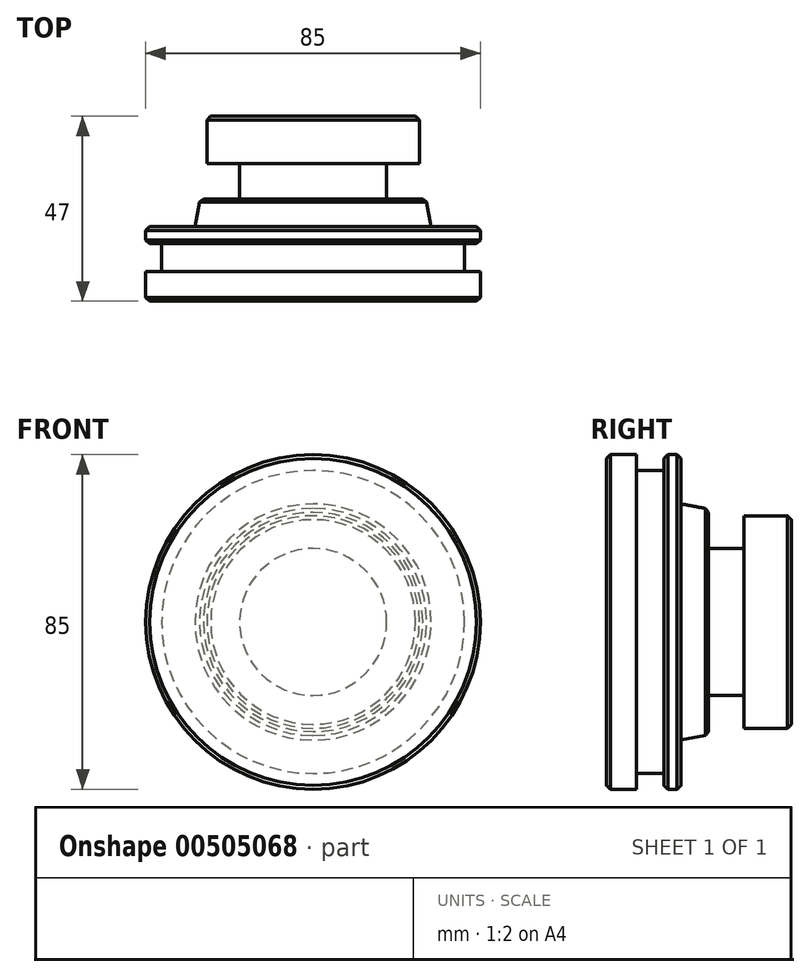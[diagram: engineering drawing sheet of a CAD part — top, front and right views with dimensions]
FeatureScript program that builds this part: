
annotation { "Feature Type Name" : "Feature", "Feature Type Description" : "" }
export const myFeature = defineFeature(function(context is Context, id is Id, definition is map)
    precondition{}
    {
        {
            var Q0;
            Q0=qCreatedBy(makeId("Front.planeOp"),FACE);
            var sketch = newSketch(context, id + "F0", { "sketchPlane" : qUnion([Q0])});
            skCircle(sketch, "E0", {"center": v(0, 0) * mm, "radius": 42.5 * mm});
            skSolve(sketch);
        }
        {
            var Q0;
            Q0 = qSketchRegion(id + "F0", true);
            extrude(context, id + "F1", {"entities" : qUnion([Q0]), "depth" : 19 * mm});
        }
        {
            var Q0;
            Q0=qCreatedBy(makeId("Right.planeOp"),FACE);
            var sketch = newSketch(context, id + "F2", { "sketchPlane" : qUnion([Q0])});
            skLineSegment(sketch, "E1", {"start": v(0, 0) * mm, "end": v(0, 42.5) * mm, "construction": true});
            skLineSegment(sketch, "E2", {"start": v(0, 42.5) * mm, "end": v(-4.4, 42.5) * mm, "construction": true});
            skLineSegment(sketch, "E3", {"start": v(-4.4, 42.5) * mm, "end": v(-4.4, 38.5) * mm});
            skLineSegment(sketch, "E4", {"start": v(-4.4, 38.5) * mm, "end": v(-11.4, 38.5) * mm});
            skLineSegment(sketch, "E5", {"start": v(-11.4, 38.5) * mm, "end": v(-11.4, 42.5) * mm});
            skLineSegment(sketch, "E6", {"start": v(0, 0) * mm, "end": v(-24.13, 0) * mm, "construction": true});
            skLineSegment(sketch, "E7", {"start": v(-11.4, 42.5) * mm, "end": v(-4.4, 42.5) * mm});
            skSolve(sketch);
        }
        {
            var Q0;
            Q0 = qSketchRegion(id + "F2", true);
            var Q1;
            Q1=makeQuery(id+"F1.opExtrude","SWEPT_FACE",FACE,{"disambiguationData":[OSD([sQuery(id+"F0.wireOp",EDGE,"E0")])]});
            revolve(context, id + "F3", {"operationType" : NewBodyOperationType.REMOVE, "entities" : qUnion([Q0]), "axis" : qUnion([Q1]), "revolveType" : RevolveType.FULL, "oppositeDirection" : true});
        }
        {
            var Q0;
            Q0=makeQuery(id+"F1.opExtrude","CAP_FACE",FACE,{"disambiguationData":[OSD([sQuery(id+"F0.wireOp",EDGE,"E0")])],"isStart":true});
            var sketch = newSketch(context, id + "F4", { "sketchPlane" : qUnion([Q0])});
            skCircle(sketch, "E8", {"center": v(0, 0) * mm, "radius": 30 * mm});
            skSolve(sketch);
        }
        {
            var Q0;
            Q0 = qSketchRegion(id + "F4", true);
            extrude(context, id + "F5", {"entities" : qUnion([Q0]), "operationType" : NewBodyOperationType.ADD, "depth" : 16 * mm});
        }
        {
            var Q0;
            Q0=makeQuery(id+"F5.opExtrude","CAP_FACE",FACE,{"disambiguationData":[OSD([sQuery(id+"F4.wireOp",EDGE,"E8")])],"isStart":false});
            var sketch = newSketch(context, id + "F6", { "sketchPlane" : qUnion([Q0])});
            skCircle(sketch, "E9", {"center": v(0, 0) * mm, "radius": 27 * mm});
            skSolve(sketch);
        }
        {
            var Q0;
            Q0 = qSketchRegion(id + "F6", true);
            extrude(context, id + "F7", {"entities" : qUnion([Q0]), "operationType" : NewBodyOperationType.ADD, "depth" : 12 * mm});
        }
        {
            var Q0;
            Q0=qCreatedBy(makeId("Top.planeOp"),FACE);
            var sketch = newSketch(context, id + "F8", { "sketchPlane" : qUnion([Q0])});
            skLineSegment(sketch, "E10", {"start": v(0, 0) * mm, "end": v(-30, 0) * mm, "construction": true});
            skLineSegment(sketch, "E11", {"start": v(0, 0) * mm, "end": v(0, 16) * mm, "construction": true});
            skLineSegment(sketch, "E12", {"start": v(0, 16) * mm, "end": v(-27, 16) * mm, "construction": true});
            skLineSegment(sketch, "E13", {"start": v(-30, 0) * mm, "end": v(-28.69, 7) * mm});
            skLineSegment(sketch, "E14", {"start": v(-30, 16) * mm, "end": v(-30, 0) * mm});
            skLineSegment(sketch, "E15", {"start": v(0, 0) * mm, "end": v(0, 46.41) * mm, "construction": true});
            skLineSegment(sketch, "E16", {"start": v(-27, 16) * mm, "end": v(-27, 7) * mm, "construction": true});
            skLineSegment(sketch, "E17", {"start": v(-28.69, 7) * mm, "end": v(-18.69, 7) * mm});
            skLineSegment(sketch, "E18", {"start": v(-18.69, 7) * mm, "end": v(-18.69, 16) * mm});
            skLineSegment(sketch, "E19", {"start": v(-18.69, 16) * mm, "end": v(-30, 16) * mm});
            skSolve(sketch);
        }
        {
            var Q0;
            Q0 = qSketchRegion(id + "F8", true);
            var Q1;
            Q1=sQuery(id+"F8.wireOp",EDGE,"E13");
            var Q2;
            Q2=sQuery(id+"F8.wireOp",EDGE,"E14");
            var Q3;
            Q3=sQuery(id+"F8.wireOp",EDGE,"Bem9fb8M-xfDn-7svO-rLqh-bTkrtEkM8QLy");
            var Q4;
            Q4=sQuery(id+"F8.wireOp",EDGE,"E15");
            revolve(context, id + "F9", {"operationType" : NewBodyOperationType.REMOVE, "entities" : qUnion([Q0]), "surfaceEntities" : qUnion([Q1, Q2, Q3]), "axis" : qUnion([Q4]), "revolveType" : RevolveType.FULL, "oppositeDirection" : true});
        }
        {
            var Q0;
            Q0=makeQuery(id+"F3.boolean.opBoolean","COPY",EDGE,{"derivedFrom":makeQuery(id+"F3.opRevolve","SWEPT_EDGE",EDGE,{"disambiguationData":[OSD([sQuery(id+"F2.wireOp",EDGE,"E3"),sQuery(id+"F2.wireOp",EDGE,"E7")])]})});
            var Q1;
            Q1=makeQuery(id+"F3.boolean.opBoolean","COPY",EDGE,{"derivedFrom":makeQuery(id+"F3.opRevolve","SWEPT_EDGE",EDGE,{"disambiguationData":[OSD([sQuery(id+"F2.wireOp",EDGE,"E5"),sQuery(id+"F2.wireOp",EDGE,"E7")])]})});
            var Q2;
            Q2=makeQuery(id+"F1.opExtrude","CAP_EDGE",EDGE,{"disambiguationData":[OSD([sQuery(id+"F0.wireOp",EDGE,"E0")])],"isStart":false});
            var Q3;
            {var subQ0=sQuery(id+"F0.wireOp",EDGE,"E0");Q3=makeQuery(id+"F3.boolean.opBoolean","SPLIT",FACE,{"disambiguationData":[TD([makeQuery(id+"F1.opExtrude","CAP_FACE",FACE,{"disambiguationData":[OSD([subQ0])],"isStart":true})])],"derivedFrom":makeQuery(id+"F1.opExtrude","SWEPT_FACE",FACE,{"disambiguationData":[OSD([subQ0])]})});}
            var Q4;
            Q4=makeQuery(id+"F9.boolean.opBoolean","COPY",EDGE,{"derivedFrom":makeQuery(id+"F9.opRevolve","SWEPT_EDGE",EDGE,{"disambiguationData":[OSD([sQuery(id+"F8.wireOp",EDGE,"E13"),sQuery(id+"F8.wireOp",EDGE,"E17")])]})});
            var Q5;
            Q5=makeQuery(id+"F7.opExtrude","CAP_EDGE",EDGE,{"disambiguationData":[OSD([sQuery(id+"F6.wireOp",EDGE,"E9")])],"isStart":true});
            var Q6;
            Q6=makeQuery(id+"F7.opExtrude","CAP_EDGE",EDGE,{"disambiguationData":[OSD([sQuery(id+"F6.wireOp",EDGE,"E9")])],"isStart":false});
            chamfer(context, id + "F10", {"entities" : qUnion([Q0, Q1, Q2, Q3, Q4, Q5, Q6]), "width" : 1 * mm, "tangentPropagation" : true});
        }
    });
